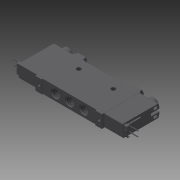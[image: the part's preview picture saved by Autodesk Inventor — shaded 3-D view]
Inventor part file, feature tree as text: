
AUTODESK INVENTOR PART (.ipt)
format: ipt  version: 2018 (Build 220112000, 112)  size: 652,800 bytes
history: native  units: mm
features: other x105, sketch x58, extrude x43, revolve x13, thread x3, hole x2
ambient origin geometry x8: Origin, YZ Plane, XZ Plane, XY Plane, X Axis, Y Axis, Z Axis, Center Point
bodies: Solid1 (feature_tree)
feature tree (224):
  extrude  "Extrusion1"  Depth=12.0mm TaperAngle=0.0deg
  extrude  "Extrusion2"  TaperAngle=360.0deg  [1 undecoded]
  extrude  "Extrusion3"  TaperAngle=360.0deg  [1 undecoded]
  sketch  "Sketch_5"  dims[d4=12.0mm d5=0.0mm d6=360.0deg]
  sketch  "Sketch_6"  dims[d7=5.4585mm d8=0.0mm d9=360.0deg]
  sketch  "Sketch_7"  dims[d10=5.4585mm d11=0.0mm d12=360.0deg d13=5.4585mm d14=0.0mm]
  revolve  "Revolution1"  Angle=360.0deg
  thread  "Thread1"  [1 undecoded]
  revolve  "Revolution2"  [1 undecoded]
  thread  "Thread2"  [1 undecoded]
  revolve  "Revolution3"  [1 undecoded]
  thread  "Thread3"  [1 undecoded]
  hole  "Hole1"  [1 undecoded]
  hole  "Hole2"  [1 undecoded]
  extrude  "Extrusion4"  Depth=4.0mm TaperAngle=0.0deg
  sketch  "Sketch_19"  dims[d43=7.7mm d44=0.0mm d45=7.7mm d46=0.0mm]
  extrude  "Extrusion5"  Depth=64.0mm TaperAngle=0.0deg
  extrude  "Extrusion6"  Depth=12.0mm TaperAngle=0.0deg
  extrude  "Extrusion7"  Depth=16.0mm TaperAngle=0.0deg
  extrude  "Extrusion8"  Depth=6.0mm TaperAngle=0.0deg
  extrude  "Extrusion9"  Depth=1.0mm TaperAngle=0.0deg
  extrude  "Extrusion10"  Depth=7.7mm TaperAngle=0.0deg
  extrude  "Extrusion11"  TaperAngle=360.0deg  [1 undecoded]
  extrude  "Extrusion12"  Depth=3.0mm TaperAngle=0.0deg
  revolve  "Revolution4"  Angle=360.0deg
  extrude  "Extrusion13"  TaperAngle=360.0deg  [1 undecoded]
  extrude  "Extrusion14"  TaperAngle=360.0deg  [1 undecoded]
  extrude  "Extrusion15"  Depth=2.15mm TaperAngle=0.0deg
  extrude  "Extrusion16"  Depth=2.1mm TaperAngle=0.0deg
  extrude  "Extrusion17"  Depth=1.5mm TaperAngle=0.0deg
  extrude  "Extrusion18"  Depth=3.0mm TaperAngle=0.0deg
  extrude  "Extrusion19"  Depth=3.0mm TaperAngle=0.0deg
  extrude  "Extrusion20"  Depth=2.0mm TaperAngle=0.0deg
  extrude  "Extrusion21"  Depth=2.0mm TaperAngle=0.0deg
  extrude  "Extrusion22"  Depth=2.0mm TaperAngle=0.0deg
  extrude  "Extrusion23"  TaperAngle=0.0deg  [1 undecoded]
  extrude  "Extrusion24"  TaperAngle=0.0deg  [1 undecoded]
  extrude  "Extrusion25"  [1 undecoded]
  revolve  "Revolution5"  [1 undecoded]
  revolve  "Revolution6"  [1 undecoded]
  revolve  "Revolution7"  [1 undecoded]
  sketch  "Sketch_59"  dims[d97=1.5mm d98=0.0mm d99=3.0mm d100=0.0mm]
  sketch  "Sketch_56"  dims[d86=360.0deg d87=2.15mm d88=0.0mm]
  extrude  "Extrusion26"  [1 undecoded]
  extrude  "Extrusion27"  [1 undecoded]
  revolve  "Revolution8"  [1 undecoded]
  revolve  "Revolution9"  [1 undecoded]
  revolve  "Revolution10"  [1 undecoded]
  revolve  "Revolution11"  [1 undecoded]
  revolve  "Revolution12"  [1 undecoded]
  revolve  "Revolution13"  [1 undecoded]
  extrude  "Extrusion28"  [1 undecoded]
  extrude  "Extrusion29"  [1 undecoded]
  extrude  "Extrusion30"  [1 undecoded]
  extrude  "Extrusion31"  [1 undecoded]
  extrude  "Extrusion32"  [1 undecoded]
  extrude  "Extrusion33"  [1 undecoded]
  extrude  "Extrusion34"  [1 undecoded]
  extrude  "Extrusion35"  [1 undecoded]
  extrude  "Extrusion36"  [1 undecoded]
  extrude  "Extrusion37"  [1 undecoded]
  extrude  "Extrusion38"  [1 undecoded]
  extrude  "Extrusion39"  [1 undecoded]
  extrude  "Extrusion40"  [1 undecoded]
  extrude  "Extrusion41"  [1 undecoded]
  extrude  "Extrusion42"  [1 undecoded]
  extrude  "Extrusion43"  [1 undecoded]
  other  "DICHTUNG_XY"
  other  "DICHTUNG_YZ"
  other  "DICHTUNG_ZX"
  other  "DICHTUNG_X"
  other  "DICHTUNG_Y"
  other  "DICHTUNG_Z"
  other  "DICHTUNG_Center"
  other  "GEHAUSE_XY"
  other  "GEHAUSE_YZ"
  other  "GEHAUSE_ZX"
  other  "GEHAUSE_X"
  other  "GEHAUSE_Y"
  other  "GEHAUSE_Z"
  other  "GEHAUSE_Center"
  other  "HHB1_XY"
  other  "HHB1_YZ"
  other  "HHB1_ZX"
  other  "HHB1_X"
  other  "HHB1_Y"
  other  "HHB1_Z"
  other  "HHB1_Center"
  other  "HHB2_XY"
  other  "HHB2_YZ"
  other  "HHB2_ZX"
  other  "HHB2_X"
  other  "HHB2_Y"
  other  "HHB2_Z"
  other  "HHB2_Center"
  other  "NEBV1_XY"
  other  "NEBV1_YZ"
  other  "NEBV1_ZX"
  other  "NEBV1_X"
  other  "NEBV1_Y"
  other  "NEBV1_Z"
  other  "NEBV1_Center"
  other  "NEBV2_XY"
  other  "NEBV2_YZ"
  other  "NEBV2_ZX"
  other  "NEBV2_X"
  other  "NEBV2_Y"
  other  "NEBV2_Z"
  other  "NEBV2_Center"
  other  "QS1_XY"
  other  "QS1_YZ"
  other  "QS1_ZX"
  other  "QS1_X"
  other  "QS1_Y"
  other  "QS1_Z"
  other  "QS1_Center"
  other  "QS2_XY"
  other  "QS2_YZ"
  other  "QS2_ZX"
  other  "QS2_X"
  other  "QS2_Y"
  other  "QS2_Z"
  other  "QS2_Center"
  other  "QSZ_XY"
  other  "QSZ_YZ"
  other  "QSZ_ZX"
  other  "QSZ_X"
  other  "QSZ_Y"
  other  "QSZ_Z"
  other  "QSZ_Center"
  other  "SCREW1_XY"
  other  "SCREW1_YZ"
  other  "SCREW1_ZX"
  other  "SCREW1_X"
  other  "SCREW1_Y"
  other  "SCREW1_Z"
  other  "SCREW1_Center"
  other  "SCREW2_XY"
  other  "SCREW2_YZ"
  other  "SCREW2_ZX"
  other  "SCREW2_X"
  other  "SCREW2_Y"
  other  "SCREW2_Z"
  other  "SCREW2_Center"
  other  "U1_XY"
  other  "U1_YZ"
  other  "U1_ZX"
  other  "U1_X"
  other  "U1_Y"
  other  "U1_Z"
  other  "U1_Center"
  other  "U2_XY"
  other  "U2_YZ"
  other  "U2_ZX"
  other  "U2_X"
  other  "U2_Y"
  other  "U2_Z"
  other  "U2_Center"
  other  "VAVE1_XY"
  other  "VAVE1_YZ"
  other  "VAVE1_ZX"
  other  "VAVE1_X"
  other  "VAVE1_Y"
  other  "VAVE1_Z"
  other  "VAVE1_Center"
  other  "VAVE2_XY"
  other  "VAVE2_YZ"
  other  "VAVE2_ZX"
  other  "VAVE2_X"
  other  "VAVE2_Y"
  other  "VAVE2_Z"
  other  "VAVE2_Center"
  sketch  "Sketch_53"  dims[d84=360.0deg d85=360.0deg]
  sketch  "Sketch_143"
  sketch  "Sketch_142"
  sketch  "Sketch7"  dims[d15=5.917468mm d16=6.5415mm d17=7.0mm d18=2.0mm d19=90.0deg d20=6.8mm d21=0.0mm]
  sketch  "Sketch8"  dims[d22=5.917468mm d23=6.5415mm d24=7.0mm d25=2.0mm d26=90.0deg d27=6.8mm d28=0.0mm d29=33.1mm d30=0.0mm d31=5.0mm d32=0.0mm]
  sketch  "Sketch_17"  dims[d39=2.4mm d40=0.0mm d41=1.0mm d42=0.0mm]
  sketch  "Sketch_30"  dims[d58=5.0mm d59=0.0mm d60=16.0mm d61=0.0mm]
  sketch  "Sketch_22"  dims[d50=33.1mm d51=0.0mm d52=64.0mm d53=0.0mm]
  sketch  "Sketch_23"  dims[d54=4.0mm d55=0.0mm d56=12.0mm d57=0.0mm]
  sketch  "Sketch_120"
  sketch  "Sketch_126"
  sketch  "Sketch_123"
  sketch  "Sketch_124"
  sketch  "Sketch_125"
  sketch  "Sketch_21"  dims[d47=360.0deg d48=4.0mm d49=0.0mm]
  sketch  "Sketch_31"  dims[d62=21.34mm d63=0.0mm d64=6.0mm d65=0.0mm]
  sketch  "Sketch_32"  dims[d66=2.4mm d67=0.0mm d68=1.0mm d69=0.0mm]
  sketch  "Sketch_119"
  sketch  "Sketch_36"  dims[d76=360.0deg d77=3.0mm d78=0.0mm]
  sketch  "Sketch_37"  dims[d79=3.0mm d80=0.0mm d81=360.0deg]
  sketch  "Sketch_35"  dims[d74=360.0deg d75=360.0deg]
  sketch  "Sketch_38"  dims[d82=360.0deg d83=360.0deg]
  sketch  "Sketch_127"
  sketch  "Sketch_128"
  sketch  "Sketch_129"
  sketch  "Sketch_130"
  sketch  "Sketch_131"
  sketch  "Sketch_34"  dims[d70=7.7mm d71=0.0mm d72=7.7mm d73=0.0mm]
  sketch  "Sketch_4"  dims[d0=33.8mm d1=0.0mm d2=12.0mm d3=0.0mm]
  sketch  "Sketch_61"  dims[d105=3.0mm d106=0.0mm d107=2.0mm d108=0.0mm]
  sketch  "Sketch_57"  dims[d89=2.15mm d90=0.0mm d91=2.1mm d92=0.0mm]
  sketch  "Sketch_62"  dims[d109=2.0mm d110=0.0mm d111=2.0mm d112=0.0mm]
  sketch  "Sketch_58"  dims[d93=2.1mm d94=0.0mm d95=1.5mm d96=0.0mm]
  sketch  "Sketch_63"  dims[d113=2.0mm d114=0.0mm d115=2.0mm d116=0.0mm]
  sketch  "Sketch_64"  dims[d117=2.0mm d118=0.0mm d119=0.0mm]
  sketch  "Sketch_65"  dims[d120=0.0mm d121=0.0mm]
  sketch  "Sketch_60"  dims[d101=3.0mm d102=0.0mm d103=3.0mm d104=0.0mm]
  sketch  "Sketch_66"  dims[d122=0.0mm]
  sketch  "Sketch_84"
  sketch  "Sketch_81"
  sketch  "Sketch_132"
  sketch  "Sketch_133"
  sketch  "Sketch_134"
  sketch  "Sketch_135"
  sketch  "Sketch_136"
  sketch  "Sketch_137"
  sketch  "Sketch_12"  dims[d33=12.0mm d34=0.0mm d35=21.34mm d36=0.0mm d37=3.0mm d38=0.0mm]
  sketch  "Sketch_68"
  sketch  "Sketch_101"
  sketch  "Sketch_102"
  sketch  "Sketch_103"
  sketch  "Sketch_104"
note: 42 required parameter values undecoded (feature->parameter linkage not recoverable at this tier; creation-order binding heuristic only, values carry confidence <= 0.55)